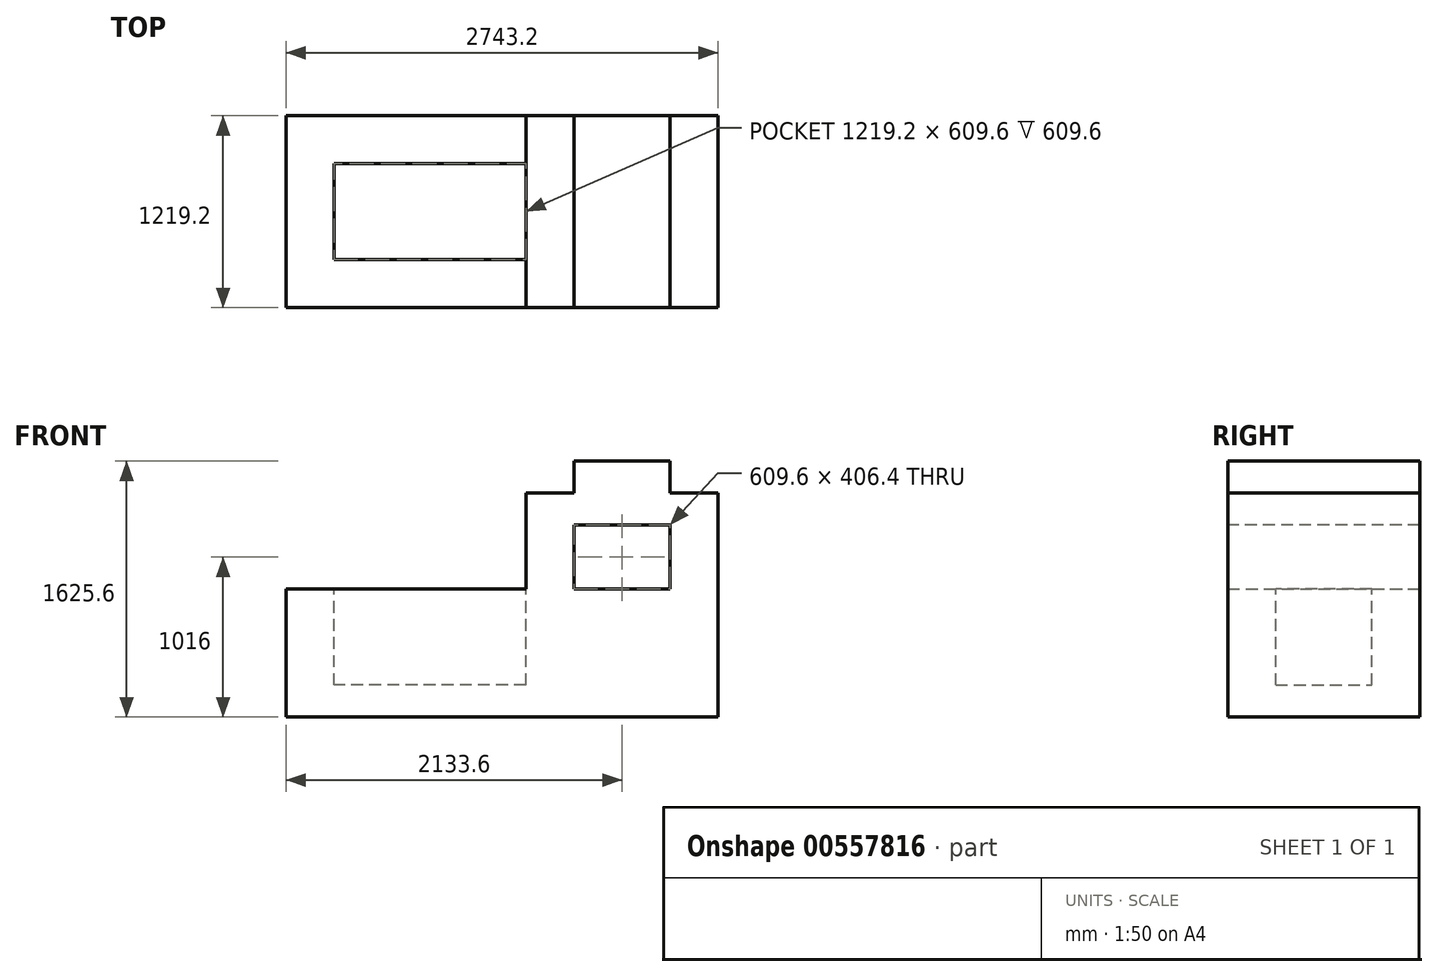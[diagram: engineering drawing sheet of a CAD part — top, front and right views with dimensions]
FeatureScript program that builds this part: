
annotation { "Feature Type Name" : "Feature", "Feature Type Description" : "" }
export const myFeature = defineFeature(function(context is Context, id is Id, definition is map)
    precondition{}
    {
        {
            var Q0;
            Q0=qCreatedBy(makeId("Front.planeOp"),FACE);
            var sketch = newSketch(context, id + "F0", { "sketchPlane" : qUnion([Q0])});
            skLineSegment(sketch, "E0", {"start": v(-376.15, -144.43) * mm, "end": v(2367.05, -144.43) * mm});
            skLineSegment(sketch, "E1", {"start": v(2367.05, -144.43) * mm, "end": v(2367.05, 1277.97) * mm});
            skLineSegment(sketch, "E2", {"start": v(2367.05, 1277.97) * mm, "end": v(2062.25, 1277.97) * mm});
            skLineSegment(sketch, "E3", {"start": v(2062.25, 1277.97) * mm, "end": v(2062.25, 1481.17) * mm});
            skLineSegment(sketch, "E4", {"start": v(2062.25, 1481.17) * mm, "end": v(1452.65, 1481.17) * mm});
            skLineSegment(sketch, "E5", {"start": v(1452.65, 1481.17) * mm, "end": v(1452.65, 1277.97) * mm});
            skLineSegment(sketch, "E6", {"start": v(1452.65, 1277.97) * mm, "end": v(1147.85, 1277.97) * mm});
            skLineSegment(sketch, "E7", {"start": v(1147.85, 1277.97) * mm, "end": v(1147.85, 668.37) * mm});
            skLineSegment(sketch, "E8", {"start": v(1147.85, 668.37) * mm, "end": v(-376.15, 668.37) * mm});
            skLineSegment(sketch, "E9", {"start": v(-376.15, 668.37) * mm, "end": v(-376.15, -144.43) * mm});
            skSolve(sketch);
        }
        {
            var Q0;
            Q0=makeQuery(id+"F0.imprint","IMPRINT",FACE,{"disambiguationData":[TD([[makeQuery(id+"F0.imprint","IMPRINT",EDGE,{"derivedFrom":sQuery(id+"F0.wireOp",EDGE,"E0")}),1.0]])]});
            extrude(context, id + "F1", {"entities" : qUnion([Q0]), "depth" : 1219.2 * mm, "offsetDistance" : 25.4 * mm});
        }
        {
            var Q0;
            Q0=makeQuery(id+"F1.opExtrude","CAP_FACE",FACE,{"disambiguationData":[OSD([sQuery(id+"F0.wireOp",EDGE,"E0"),sQuery(id+"F0.wireOp",EDGE,"E1"),sQuery(id+"F0.wireOp",EDGE,"E2"),sQuery(id+"F0.wireOp",EDGE,"E3"),sQuery(id+"F0.wireOp",EDGE,"E4"),sQuery(id+"F0.wireOp",EDGE,"E5"),sQuery(id+"F0.wireOp",EDGE,"E6"),sQuery(id+"F0.wireOp",EDGE,"E7"),sQuery(id+"F0.wireOp",EDGE,"E8"),sQuery(id+"F0.wireOp",EDGE,"E9")])],"isStart":false});
            var sketch = newSketch(context, id + "F2", { "sketchPlane" : qUnion([Q0])});
            skLineSegment(sketch, "E10.bottom", {"start": v(1452.65, 1074.77) * mm, "end": v(2062.25, 1074.77) * mm});
            skLineSegment(sketch, "E10.top", {"start": v(1452.65, 668.37) * mm, "end": v(2062.25, 668.37) * mm});
            skLineSegment(sketch, "E10.left", {"start": v(1452.65, 1074.77) * mm, "end": v(1452.65, 668.37) * mm});
            skLineSegment(sketch, "E10.right", {"start": v(2062.25, 1074.77) * mm, "end": v(2062.25, 668.37) * mm});
            skSolve(sketch);
        }
        {
            var Q0;
            Q0=makeQuery(id+"F2.imprint","IMPRINT",FACE,{"disambiguationData":[TD([[makeQuery(id+"F2.imprint","IMPRINT",EDGE,{"derivedFrom":sQuery(id+"F2.wireOp",EDGE,"E10.bottom")}),-1.0]])]});
            extrude(context, id + "F3", {"entities" : qUnion([Q0]), "operationType" : NewBodyOperationType.REMOVE, "endBound" : BoundingType.THROUGH_ALL, "oppositeDirection" : true, "depth" : 25.4 * mm, "offsetDistance" : 25.4 * mm});
        }
        {
            var Q0;
            Q0=makeQuery(id+"F1.opExtrude","SWEPT_FACE",FACE,{"disambiguationData":[OSD([sQuery(id+"F0.wireOp",EDGE,"E8")])]});
            var sketch = newSketch(context, id + "F4", { "sketchPlane" : qUnion([Q0])});
            skLineSegment(sketch, "E11.bottom", {"start": v(1147.85, -304.8) * mm, "end": v(-71.35, -304.8) * mm});
            skLineSegment(sketch, "E11.top", {"start": v(1147.85, -914.4) * mm, "end": v(-71.35, -914.4) * mm});
            skLineSegment(sketch, "E11.left", {"start": v(1147.85, -304.8) * mm, "end": v(1147.85, -914.4) * mm});
            skLineSegment(sketch, "E11.right", {"start": v(-71.35, -304.8) * mm, "end": v(-71.35, -914.4) * mm});
            skSolve(sketch);
        }
        {
            var Q0;
            Q0=makeQuery(id+"F4.imprint","IMPRINT",FACE,{"disambiguationData":[TD([[makeQuery(id+"F4.imprint","IMPRINT",EDGE,{"derivedFrom":sQuery(id+"F4.wireOp",EDGE,"E11.bottom")}),1.0]])]});
            extrude(context, id + "F5", {"entities" : qUnion([Q0]), "operationType" : NewBodyOperationType.REMOVE, "oppositeDirection" : true, "depth" : 609.6 * mm, "offsetDistance" : 25.4 * mm});
        }
    });
